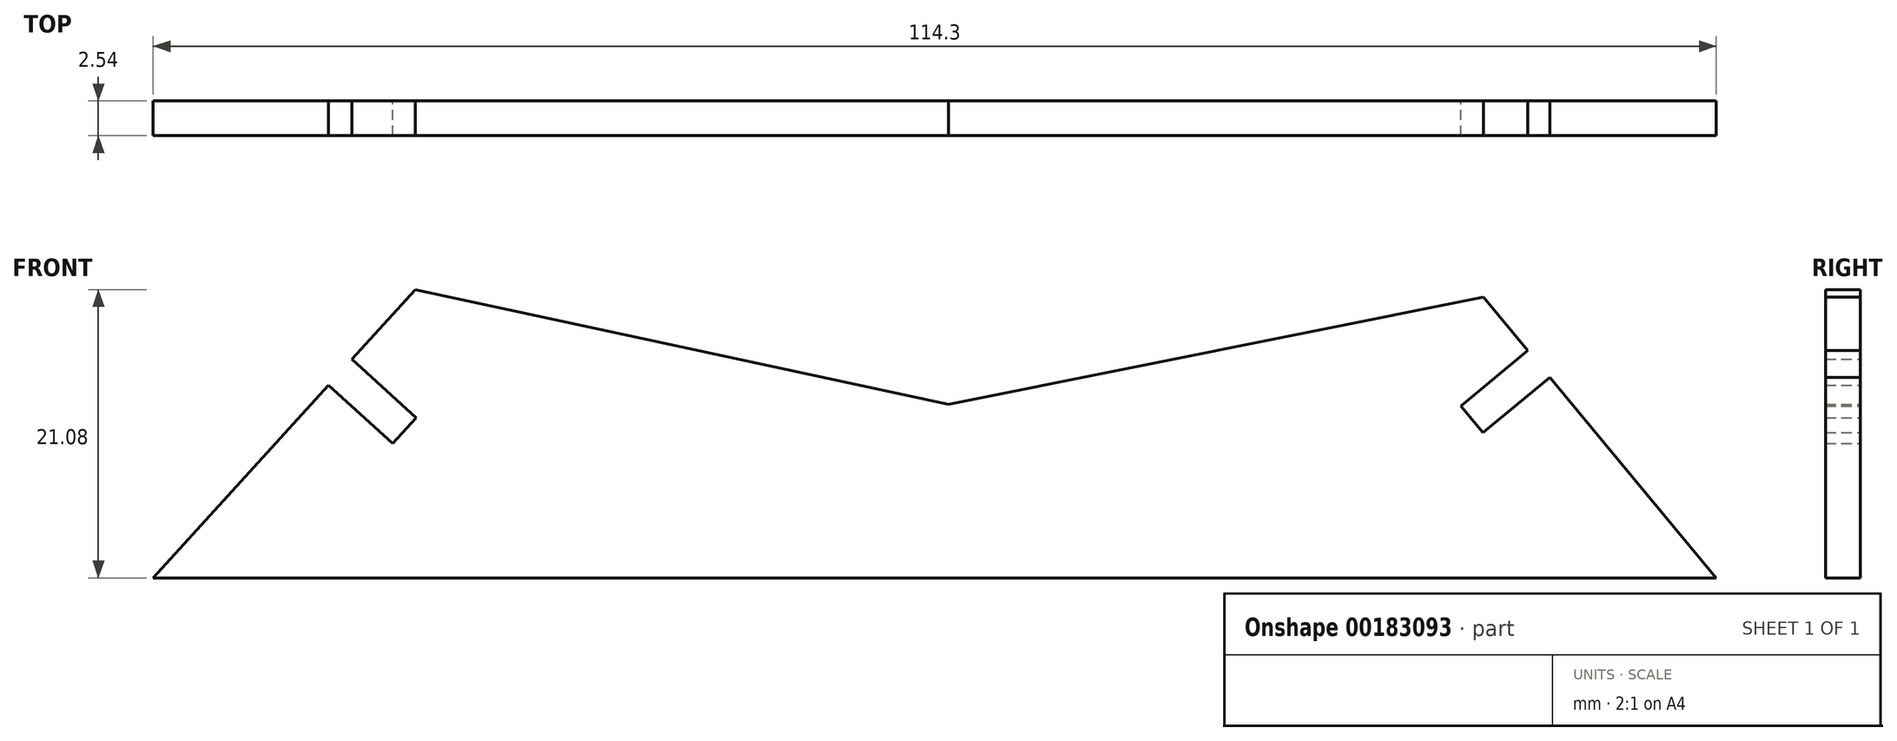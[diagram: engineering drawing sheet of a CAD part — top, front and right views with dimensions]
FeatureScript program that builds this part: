
annotation { "Feature Type Name" : "Feature", "Feature Type Description" : "" }
export const myFeature = defineFeature(function(context is Context, id is Id, definition is map)
    precondition{}
    {
        {
            var Q0;
            Q0=qCreatedBy(makeId("Front.planeOp"),FACE);
            var sketch = newSketch(context, id + "F0", { "sketchPlane" : qUnion([Q0])});
            skLineSegment(sketch, "E0", {"start": v(0, 0) * mm, "end": v(39.12, 7.84) * mm});
            skLineSegment(sketch, "E1", {"start": v(39.12, 7.84) * mm, "end": v(42.36, 3.92) * mm});
            skLineSegment(sketch, "E2", {"start": v(56.14, -12.7) * mm, "end": v(-58.16, -12.7) * mm});
            skLineSegment(sketch, "E3", {"start": v(-58.16, -12.7) * mm, "end": v(-45.35, 1.4) * mm});
            skLineSegment(sketch, "E4", {"start": v(-39, 8.38) * mm, "end": v(0, 0) * mm});
            skLineSegment(sketch, "E5", {"start": v(-45.35, 1.4) * mm, "end": v(-40.65, -2.87) * mm});
            skLineSegment(sketch, "E6", {"start": v(-40.65, -2.87) * mm, "end": v(-38.94, -1) * mm});
            skLineSegment(sketch, "E7", {"start": v(-38.94, -1) * mm, "end": v(-43.64, 3.28) * mm});
            skLineSegment(sketch, "E8", {"start": v(42.36, 3.92) * mm, "end": v(37.47, -0.13) * mm});
            skLineSegment(sketch, "E9", {"start": v(37.47, -0.13) * mm, "end": v(39.1, -2.08) * mm});
            skLineSegment(sketch, "E10", {"start": v(39.1, -2.08) * mm, "end": v(43.98, 1.97) * mm});
            skLineSegment(sketch, "E11.trimOffspring", {"start": v(-43.64, 3.28) * mm, "end": v(-39, 8.38) * mm});
            skLineSegment(sketch, "E12.trimOffspring", {"start": v(43.98, 1.97) * mm, "end": v(56.14, -12.7) * mm});
            skSolve(sketch);
        }
        {
            var Q0;
            Q0=qSketchRegion(id+"F0",true);
            extrude(context, id + "F1", {"entities" : qUnion([Q0]), "depth" : 2.54 * mm});
        }
    });
